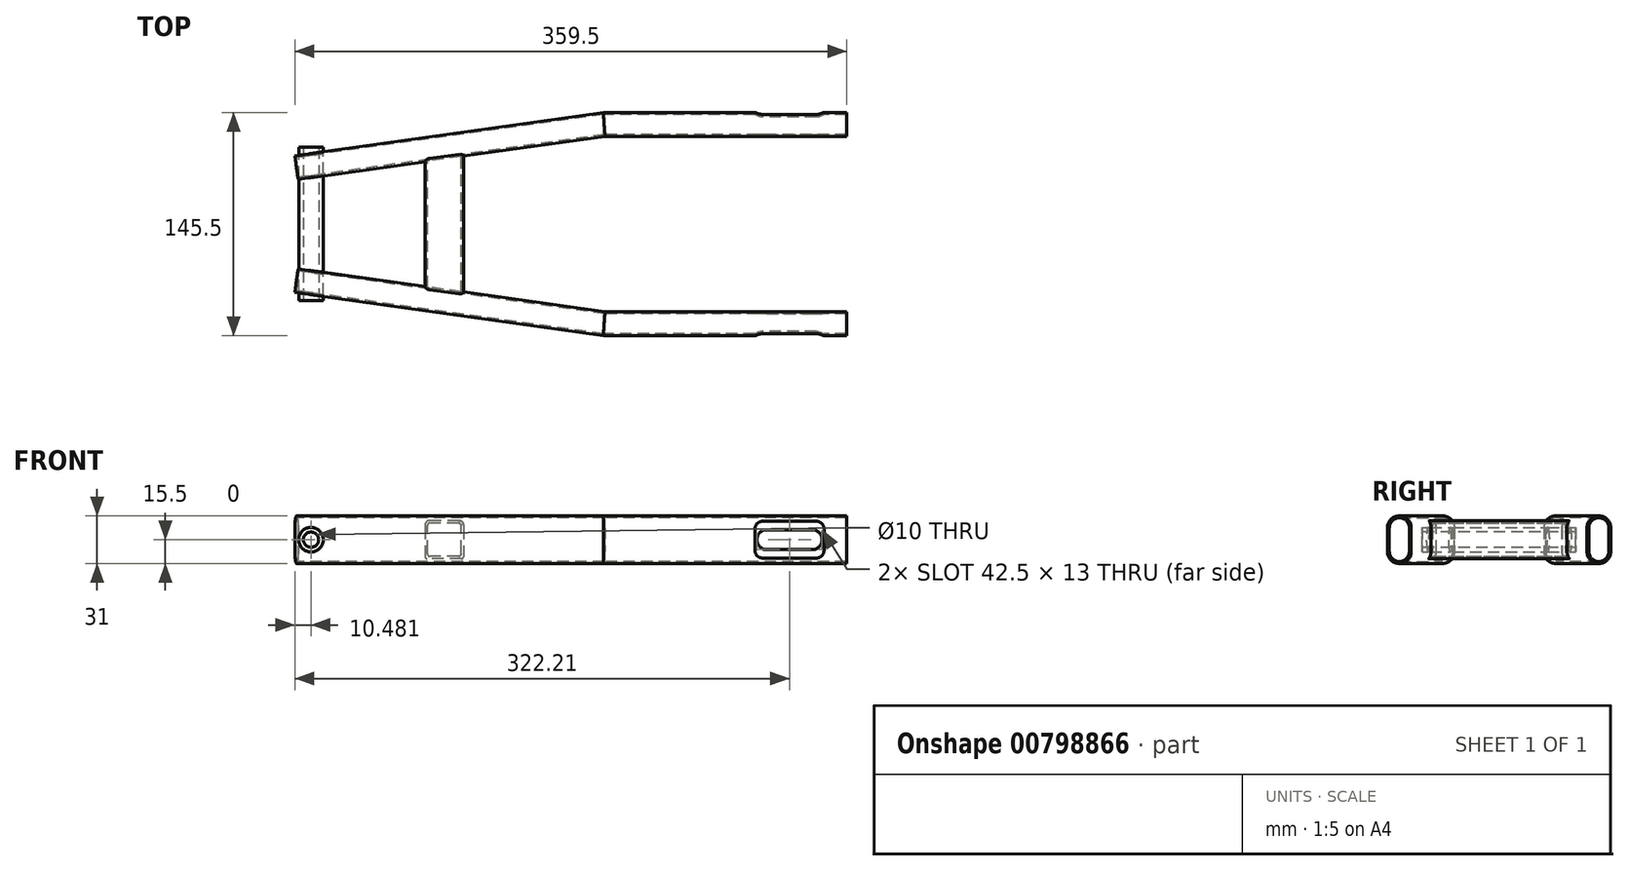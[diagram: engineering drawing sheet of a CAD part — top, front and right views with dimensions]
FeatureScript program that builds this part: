
annotation { "Feature Type Name" : "Feature", "Feature Type Description" : "" }
export const myFeature = defineFeature(function(context is Context, id is Id, definition is map)
    precondition{}
    {
        {
            var Q0;
            Q0=qCreatedBy(makeId("Top.planeOp"),FACE);
            var sketch = newSketch(context, id + "F0", { "sketchPlane" : qUnion([Q0])});
            skLineSegment(sketch, "E0", {"start": v(0, 65) * mm, "end": v(-158.03, 65) * mm});
            skLineSegment(sketch, "E1", {"start": v(-158.03, 65) * mm, "end": v(-358.42, 36.84) * mm});
            skSolve(sketch);
        }
        {
            var Q0;
            Q0=qCreatedBy(makeId("Right.planeOp"),FACE);
            var sketch = newSketch(context, id + "F1", { "sketchPlane" : qUnion([Q0])});
            skLineSegment(sketch, "E2.left", {"start": v(57.25, 7.75) * mm, "end": v(57.25, -7.75) * mm});
            skLineSegment(sketch, "E2.right", {"start": v(72.75, 7.75) * mm, "end": v(72.75, -7.75) * mm});
            skPoint(sketch, "E2.middle", {"position": v(65, 0) * mm});
            skArc(sketch, "E3", {"start": v(72.75, 7.75) * mm, "mid": v(65, 15.5) * mm, "end": v(57.25, 7.75) * mm});
            skArc(sketch, "E4", {"start": v(57.25, -7.75) * mm, "mid": v(65, -15.5) * mm, "end": v(72.75, -7.75) * mm});
            skLineSegment(sketch, "E5.0", {"start": v(58.45, 7.75) * mm, "end": v(58.45, -7.75) * mm});
            skLineSegment(sketch, "E6.0", {"start": v(71.55, 7.75) * mm, "end": v(71.55, -7.75) * mm});
            skArc(sketch, "E7.0", {"start": v(71.55, 7.75) * mm, "mid": v(65, 14.3) * mm, "end": v(58.45, 7.75) * mm});
            skArc(sketch, "E8.0", {"start": v(58.45, -7.75) * mm, "mid": v(65, -14.3) * mm, "end": v(71.55, -7.75) * mm});
            skSolve(sketch);
        }
        {
            var Q0;
            Q0 = qSketchRegion(id + "F1", true);
            var Q1;
            Q1 = qConstructionFilter(qBodyType(qCreatedBy(id + "F0" ,EDGE), BodyType.WIRE), ConstructionObject.NO);
            sweep(context, id + "F2", {"profiles" : qUnion([Q0]), "path" : qUnion([Q1])});
        }
        {
            var Q0;
            Q0=makeQuery(id+"F2.opSweep","SWEPT_FACE",FACE,{"disambiguationData":[OSD([sQuery(id+"F0.wireOp",EDGE,"E0"),sQuery(id+"F1.wireOp",EDGE,"E2.left")])]});
            var sketch = newSketch(context, id + "F3", { "sketchPlane" : qUnion([Q0])});
            skLineSegment(sketch, "E9.bottom", {"start": v(-22.54, 6.5) * mm, "end": v(-52.04, 6.5) * mm});
            skLineSegment(sketch, "E9.top", {"start": v(-22.54, -6.5) * mm, "end": v(-52.04, -6.5) * mm});
            skPoint(sketch, "E9.middle", {"position": v(-37.3, 0) * mm});
            skArc(sketch, "E10", {"start": v(-52.04, 6.5) * mm, "mid": v(-58.54, 0) * mm, "end": v(-52.04, -6.5) * mm});
            skArc(sketch, "E11", {"start": v(-22.54, 6.5) * mm, "mid": v(-16.04, 0) * mm, "end": v(-22.54, -6.5) * mm});
            skSolve(sketch);
        }
        {
            var Q0;
            Q0 = qSketchRegion(id + "F3", true);
            extrude(context, id + "F4", {"entities" : qUnion([Q0]), "operationType" : NewBodyOperationType.REMOVE, "oppositeDirection" : true, "depth" : 4 * mm, "offsetDistance" : 25 * mm});
        }
        {
            var Q0;
            Q0=makeQuery(id+"F2.opSweep","SWEPT_FACE",FACE,{"disambiguationData":[OSD([sQuery(id+"F0.wireOp",EDGE,"E0"),sQuery(id+"F1.wireOp",EDGE,"E2.right")])]});
            var sketch = newSketch(context, id + "F5", { "sketchPlane" : qUnion([Q0])});
            skLineSegment(sketch, "E12.bottom", {"start": v(54.76, 12) * mm, "end": v(19.76, 12) * mm});
            skLineSegment(sketch, "E12.top", {"start": v(54.76, -12) * mm, "end": v(19.76, -12) * mm});
            skLineSegment(sketch, "E12.left", {"start": v(59.76, 7) * mm, "end": v(59.76, -7) * mm});
            skLineSegment(sketch, "E12.right", {"start": v(14.76, 7) * mm, "end": v(14.76, -7) * mm});
            skPoint(sketch, "E12.middle", {"position": v(37.26, 0) * mm});
            skPoint(sketch, "E13.visualSharp", {"position": v(14.76, 12) * mm});
            skArc(sketch, "E13.filletArc", {"start": v(19.76, 12) * mm, "mid": v(16.22, 10.54) * mm, "end": v(14.76, 7) * mm});
            skPoint(sketch, "E14.visualSharp", {"position": v(59.76, 12) * mm});
            skArc(sketch, "E14.filletArc", {"start": v(59.76, 7) * mm, "mid": v(58.3, 10.54) * mm, "end": v(54.76, 12) * mm});
            skPoint(sketch, "E15.visualSharp", {"position": v(59.76, -12) * mm});
            skArc(sketch, "E15.filletArc", {"start": v(54.76, -12) * mm, "mid": v(58.3, -10.54) * mm, "end": v(59.76, -7) * mm});
            skPoint(sketch, "E16.visualSharp", {"position": v(14.76, -12) * mm});
            skArc(sketch, "E16.filletArc", {"start": v(14.76, -7) * mm, "mid": v(16.22, -10.54) * mm, "end": v(19.76, -12) * mm});
            skSolve(sketch);
        }
        {
            var Q0;
            Q0 = qSketchRegion(id + "F5", true);
            extrude(context, id + "F6", {"entities" : qUnion([Q0]), "operationType" : NewBodyOperationType.REMOVE, "oppositeDirection" : true, "depth" : 4 * mm, "offsetDistance" : 25 * mm});
        }
        {
            var Q0;
            Q0=makeQuery(id+"F2.opSweep","SWEPT_BODY",BODY,{"disambiguationData":[OSD([sQuery(id+"F0.wireOp",EDGE,"E1"),sQuery(id+"F1.wireOp",EDGE,"E2.left"),sQuery(id+"F1.wireOp",EDGE,"E2.right"),sQuery(id+"F1.wireOp",EDGE,"E3"),sQuery(id+"F1.wireOp",EDGE,"E4"),sQuery(id+"F1.wireOp",EDGE,"E5.0"),sQuery(id+"F1.wireOp",EDGE,"E6.0"),sQuery(id+"F1.wireOp",EDGE,"E7.0"),sQuery(id+"F1.wireOp",EDGE,"E8.0")])]});
            var Q1;
            Q1=qCreatedBy(makeId("Front.planeOp"),FACE);
            mirror(context, id + "F7", {"entities" : qUnion([Q0]), "mirrorPlane" : qUnion([Q1])});
        }
        {
            var Q0;
            Q0=qCreatedBy(makeId("Front.planeOp"),FACE);
            var sketch = newSketch(context, id + "F8", { "sketchPlane" : qUnion([Q0])});
            skCircle(sketch, "E17", {"center": v(-349.02, 0) * mm, "radius": 8 * mm});
            skSolve(sketch);
        }
        {
            var Q0;
            Q0 = qSketchRegion(id + "F8", true);
            extrude(context, id + "F9", {"entities" : qUnion([Q0]), "operationType" : NewBodyOperationType.ADD, "endBound" : BoundingType.SYMMETRIC, "depth" : 100 * mm, "offsetDistance" : 25 * mm});
        }
        {
            var Q0;
            Q0=makeQuery(id+"F9.opExtrude","CAP_FACE",FACE,{"disambiguationData":[OSD([sQuery(id+"F8.wireOp",EDGE,"E17")])],"isStart":false});
            var sketch = newSketch(context, id + "F10", { "sketchPlane" : qUnion([Q0])});
            skCircle(sketch, "E18", {"center": v(-349.02, 0) * mm, "radius": 5 * mm});
            skSolve(sketch);
        }
        {
            var Q0;
            Q0 = qSketchRegion(id + "F10", true);
            extrude(context, id + "F11", {"entities" : qUnion([Q0]), "operationType" : NewBodyOperationType.REMOVE, "endBound" : BoundingType.THROUGH_ALL, "oppositeDirection" : true, "depth" : 25 * mm, "offsetDistance" : 25 * mm});
        }
        {
            var Q0;
            Q0=qCreatedBy(makeId("Front.planeOp"),FACE);
            var sketch = newSketch(context, id + "F12", { "sketchPlane" : qUnion([Q0])});
            skLineSegment(sketch, "E19.bottom", {"start": v(-252.69, 12.5) * mm, "end": v(-271.69, 12.5) * mm});
            skLineSegment(sketch, "E19.top", {"start": v(-251.09, -12.5) * mm, "end": v(-273.29, -12.5) * mm});
            skLineSegment(sketch, "E19.left", {"start": v(-249.69, 9.5) * mm, "end": v(-249.69, -11.1) * mm});
            skLineSegment(sketch, "E19.right", {"start": v(-274.69, 9.5) * mm, "end": v(-274.69, -11.1) * mm});
            skPoint(sketch, "E19.middle", {"position": v(-262.19, 0) * mm});
            skPoint(sketch, "E20.visualSharp", {"position": v(-274.69, 12.5) * mm});
            skArc(sketch, "E20.filletArc", {"start": v(-271.69, 12.5) * mm, "mid": v(-273.81, 11.62) * mm, "end": v(-274.69, 9.5) * mm});
            skPoint(sketch, "E21.visualSharp", {"position": v(-249.69, 12.5) * mm});
            skArc(sketch, "E21.filletArc", {"start": v(-249.69, 9.5) * mm, "mid": v(-250.57, 11.62) * mm, "end": v(-252.69, 12.5) * mm});
            skPoint(sketch, "E22.visualSharp", {"position": v(-249.69, -12.5) * mm});
            skArc(sketch, "E22.filletArc", {"start": v(-251.09, -12.5) * mm, "mid": v(-250.1, -12.09) * mm, "end": v(-249.69, -11.1) * mm});
            skPoint(sketch, "E23.visualSharp", {"position": v(-274.69, -12.5) * mm});
            skArc(sketch, "E23.filletArc", {"start": v(-274.69, -11.1) * mm, "mid": v(-274.28, -12.09) * mm, "end": v(-273.29, -12.5) * mm});
            skLineSegment(sketch, "E24.0", {"start": v(-252.89, 10.9) * mm, "end": v(-271.49, 10.9) * mm});
            skLineSegment(sketch, "E25.0", {"start": v(-273.09, 9.3) * mm, "end": v(-273.09, -9.3) * mm});
            skArc(sketch, "E26.filletArc", {"start": v(-271.49, 10.9) * mm, "mid": v(-272.62, 10.43) * mm, "end": v(-273.09, 9.3) * mm});
            skLineSegment(sketch, "E27.0", {"start": v(-252.89, -10.9) * mm, "end": v(-271.49, -10.9) * mm});
            skLineSegment(sketch, "E28.0", {"start": v(-251.29, 9.3) * mm, "end": v(-251.29, -9.3) * mm});
            skArc(sketch, "E29.filletArc", {"start": v(-251.29, 9.3) * mm, "mid": v(-251.76, 10.43) * mm, "end": v(-252.89, 10.9) * mm});
            skArc(sketch, "E30.filletArc", {"start": v(-273.09, -9.3) * mm, "mid": v(-272.62, -10.43) * mm, "end": v(-271.49, -10.9) * mm});
            skArc(sketch, "E31.filletArc", {"start": v(-252.89, -10.9) * mm, "mid": v(-251.76, -10.43) * mm, "end": v(-251.29, -9.3) * mm});
            skSolve(sketch);
        }
        {
            var Q0;
            Q0 = qSketchRegion(id + "F12", true);
            extrude(context, id + "F13", {"entities" : qUnion([Q0]), "operationType" : NewBodyOperationType.ADD, "endBound" : BoundingType.UP_TO_NEXT, "depth" : 25 * mm, "offsetDistance" : 25 * mm, "hasSecondDirection" : true, "secondDirectionBound" : SecondDirectionBoundingType.UP_TO_NEXT, "secondDirectionOppositeDirection" : true, "secondDirectionDepth" : 25 * mm});
        }
    });
